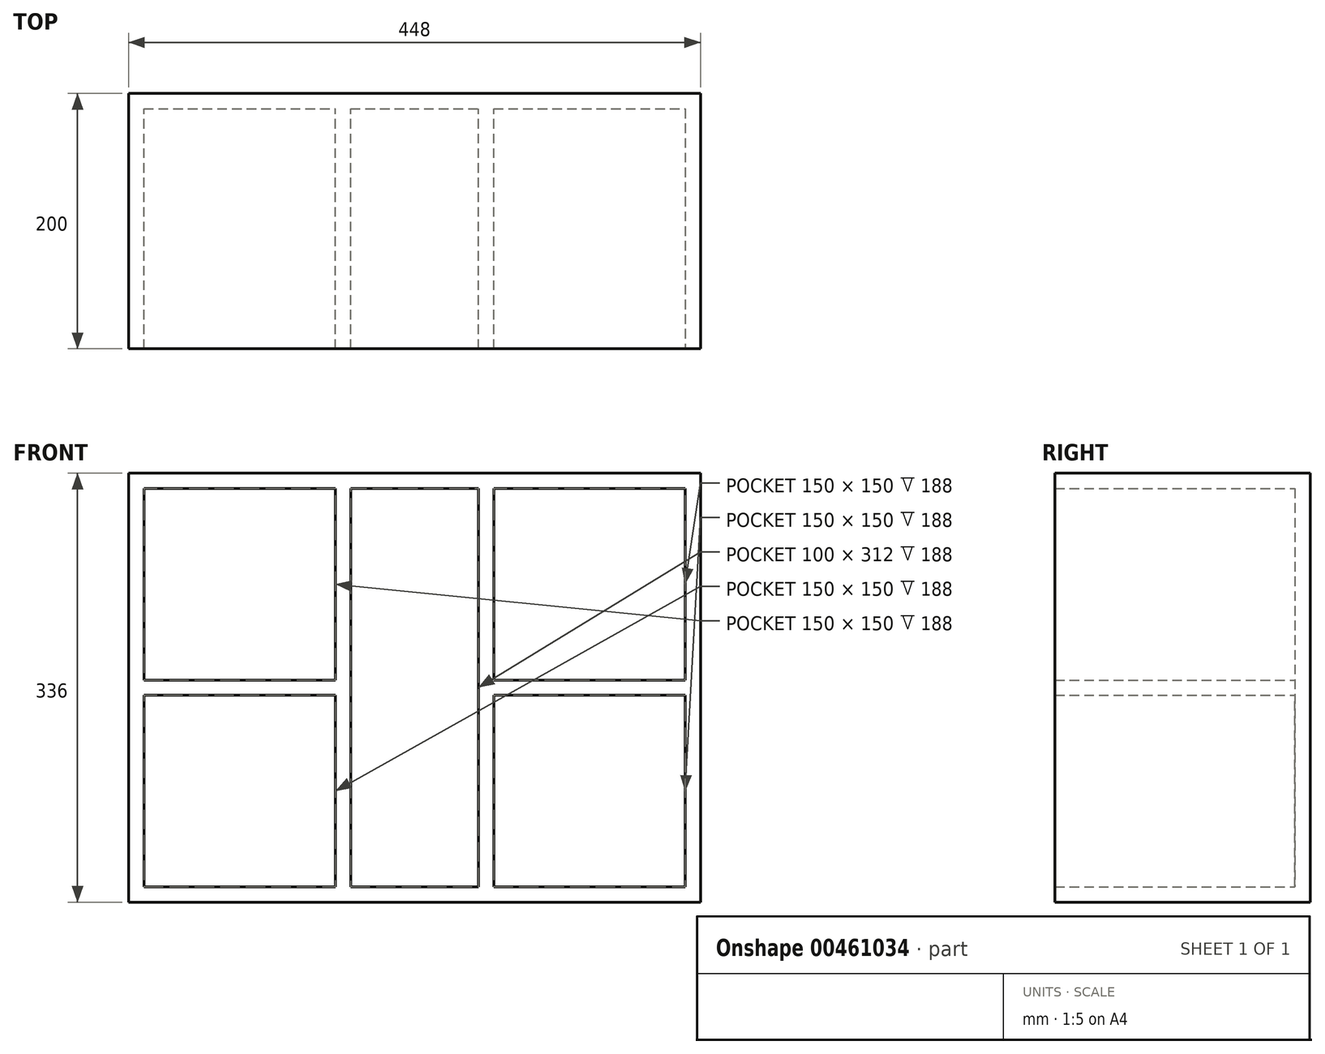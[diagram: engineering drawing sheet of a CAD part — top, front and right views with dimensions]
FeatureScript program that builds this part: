
annotation { "Feature Type Name" : "Feature", "Feature Type Description" : "" }
export const myFeature = defineFeature(function(context is Context, id is Id, definition is map)
    precondition{}
    {
        {
            var Q0;
            Q0=qCreatedBy(makeId("Front.planeOp"),FACE);
            var sketch = newSketch(context, id + "F0", { "sketchPlane" : qUnion([Q0])});
            skLineSegment(sketch, "E0.bottom", {"start": v(-224, -168) * mm, "end": v(224, -168) * mm});
            skLineSegment(sketch, "E0.top", {"start": v(-224, 168) * mm, "end": v(224, 168) * mm});
            skLineSegment(sketch, "E0.left", {"start": v(-224, -168) * mm, "end": v(-224, 168) * mm});
            skLineSegment(sketch, "E0.right", {"start": v(224, -168) * mm, "end": v(224, 168) * mm});
            skPoint(sketch, "E0.middle", {"position": v(0, 0) * mm});
            skSolve(sketch);
        }
        {
            var Q0;
            Q0=makeQuery(id+"F0.imprint","IMPRINT",FACE,{"disambiguationData":[TD([[makeQuery(id+"F0.imprint","IMPRINT",EDGE,{"derivedFrom":sQuery(id+"F0.wireOp",EDGE,"E0.bottom")}),1.0]])]});
            extrude(context, id + "F1", {"entities" : qUnion([Q0]), "oppositeDirection" : true, "offsetDistance" : 25 * mm, "depth" : 200 * mm});
        }
        {
            var Q0;
            Q0=makeQuery(id+"F1.opExtrude","CAP_FACE",FACE,{"disambiguationData":[OSD([sQuery(id+"F0.wireOp",EDGE,"E0.bottom"),sQuery(id+"F0.wireOp",EDGE,"E0.top"),sQuery(id+"F0.wireOp",EDGE,"E0.left"),sQuery(id+"F0.wireOp",EDGE,"E0.right")])],"isStart":true});
            shell(context, id + "F2", {"entities" : qUnion([Q0]), "thickness" : 12 * mm});
        }
        {
            var Q0;
            Q0=makeQuery(id+"F2.opShell","OFFSET_FACE",FACE,{"disambiguationData":[OSD([sQuery(id+"F0.wireOp",EDGE,"E0.bottom"),sQuery(id+"F0.wireOp",EDGE,"E0.top"),sQuery(id+"F0.wireOp",EDGE,"E0.left"),sQuery(id+"F0.wireOp",EDGE,"E0.right")])]});
            var sketch = newSketch(context, id + "F3", { "sketchPlane" : qUnion([Q0])});
            skLineSegment(sketch, "E1.bottom", {"start": v(-212, 156) * mm, "end": v(-62, 156) * mm});
            skLineSegment(sketch, "E1.top", {"start": v(-212, 6) * mm, "end": v(-62, 6) * mm});
            skLineSegment(sketch, "E1.left", {"start": v(-212, 156) * mm, "end": v(-212, 6) * mm});
            skLineSegment(sketch, "E1.right", {"start": v(-62, 156) * mm, "end": v(-62, 6) * mm});
            skLineSegment(sketch, "E2.bottom", {"start": v(-212, -156) * mm, "end": v(-62, -156) * mm});
            skLineSegment(sketch, "E2.top", {"start": v(-212, -6) * mm, "end": v(-62, -6) * mm});
            skLineSegment(sketch, "E2.left", {"start": v(-212, -156) * mm, "end": v(-212, -6) * mm});
            skLineSegment(sketch, "E2.right", {"start": v(-62, -156) * mm, "end": v(-62, -6) * mm});
            skLineSegment(sketch, "E3.bottom", {"start": v(-62, 156) * mm, "end": v(-50, 156) * mm});
            skLineSegment(sketch, "E3.top", {"start": v(-62, -156) * mm, "end": v(-50, -156) * mm});
            skLineSegment(sketch, "E3.left", {"start": v(-62, 156) * mm, "end": v(-62, -156) * mm});
            skLineSegment(sketch, "E3.right", {"start": v(-50, 156) * mm, "end": v(-50, -156) * mm});
            skLineSegment(sketch, "E4.bottom", {"start": v(212, 156) * mm, "end": v(62, 156) * mm});
            skLineSegment(sketch, "E4.top", {"start": v(212, 6) * mm, "end": v(62, 6) * mm});
            skLineSegment(sketch, "E4.left", {"start": v(212, 156) * mm, "end": v(212, 6) * mm});
            skLineSegment(sketch, "E4.right", {"start": v(62, 156) * mm, "end": v(62, 6) * mm});
            skLineSegment(sketch, "E5.bottom", {"start": v(212, -156) * mm, "end": v(62, -156) * mm});
            skLineSegment(sketch, "E5.top", {"start": v(212, -6) * mm, "end": v(62, -6) * mm});
            skLineSegment(sketch, "E5.left", {"start": v(212, -156) * mm, "end": v(212, -6) * mm});
            skLineSegment(sketch, "E5.right", {"start": v(62, -156) * mm, "end": v(62, -6) * mm});
            skLineSegment(sketch, "E6.bottom", {"start": v(62, 156) * mm, "end": v(50, 156) * mm});
            skLineSegment(sketch, "E6.top", {"start": v(62, -156) * mm, "end": v(50, -156) * mm});
            skLineSegment(sketch, "E6.left", {"start": v(62, 156) * mm, "end": v(62, -156) * mm});
            skLineSegment(sketch, "E6.right", {"start": v(50, 156) * mm, "end": v(50, -156) * mm});
            skSolve(sketch);
        }
        {
            var Q0;
            {var subQ0=sQuery(id+"F3.wireOp",EDGE,"E1.top");Q0=makeQuery(id+"F3.imprint","IMPRINT",FACE,{"disambiguationData":[TD([[makeQuery(id+"F3.imprint","IMPRINT",EDGE,{"derivedFrom":subQ0}),-1.0]])]});}
            var Q1;
            {var subQ3=sQuery(id+"F3.wireOp",EDGE,"E3.bottom");Q1=makeQuery(id+"F3.imprint","IMPRINT",FACE,{"disambiguationData":[TD([[makeQuery(id+"F3.imprint","IMPRINT",EDGE,{"derivedFrom":subQ3}),-1.0]])]});}
            var Q2;
            {var subQ3=sQuery(id+"F3.wireOp",EDGE,"E6.bottom");Q2=makeQuery(id+"F3.imprint","IMPRINT",FACE,{"disambiguationData":[TD([[makeQuery(id+"F3.imprint","IMPRINT",EDGE,{"derivedFrom":subQ3}),-1.0]])]});}
            var Q3;
            {var subQ0=sQuery(id+"F3.wireOp",EDGE,"E4.top");Q3=makeQuery(id+"F3.imprint","IMPRINT",FACE,{"disambiguationData":[TD([[makeQuery(id+"F3.imprint","IMPRINT",EDGE,{"derivedFrom":subQ0}),1.0]])]});}
            extrude(context, id + "F4", {"entities" : qUnion([Q0, Q1, Q2, Q3]), "operationType" : NewBodyOperationType.ADD, "offsetDistance" : 25 * mm, "depth" : 188 * mm});
        }
    });
